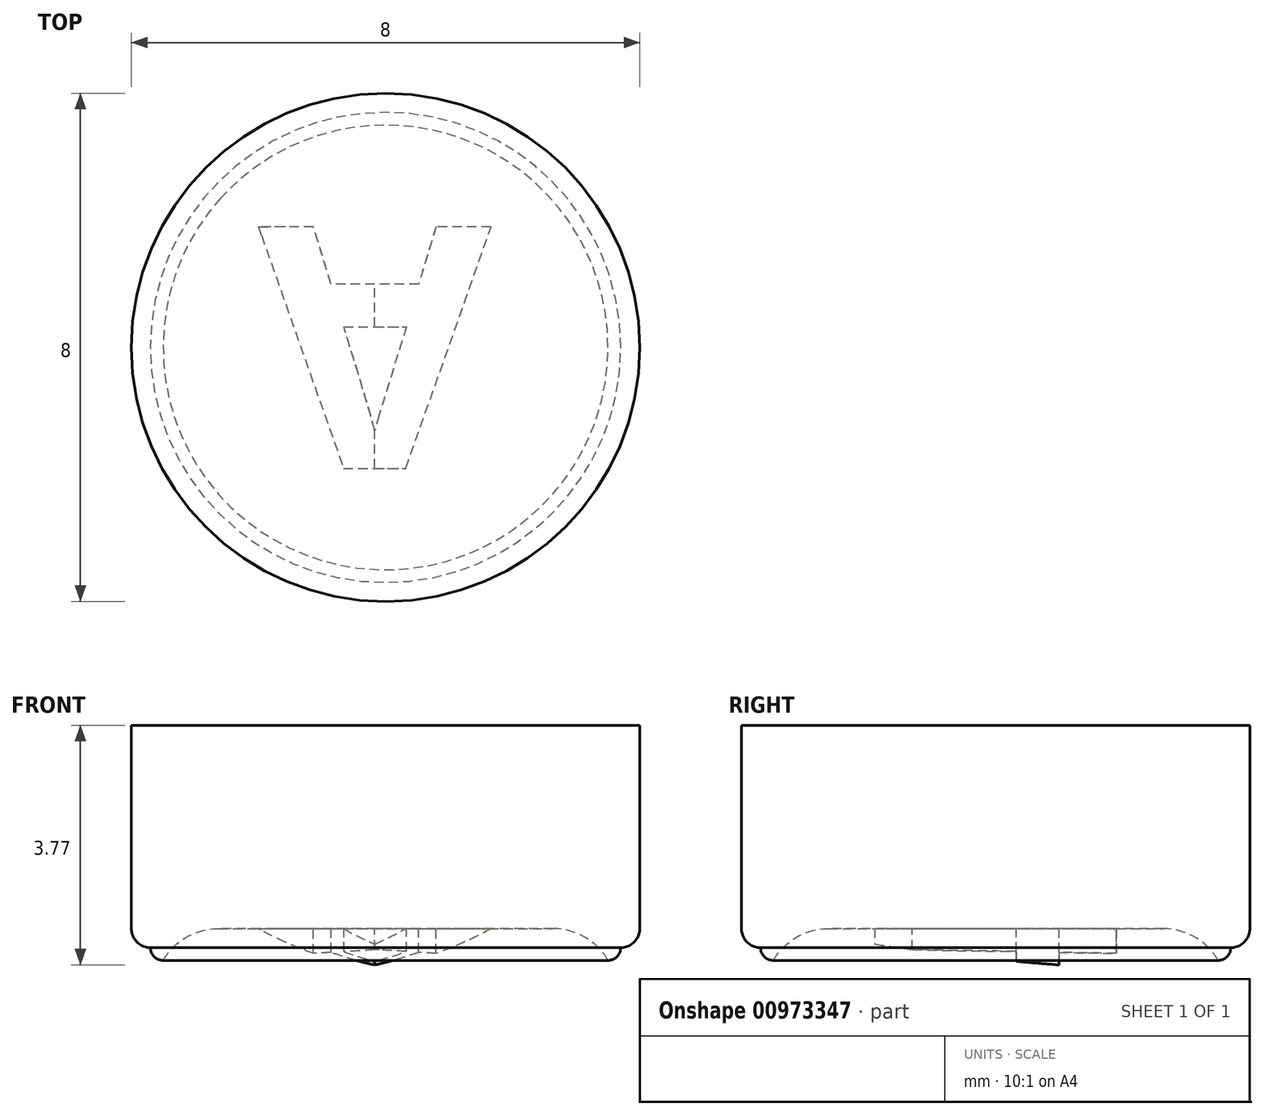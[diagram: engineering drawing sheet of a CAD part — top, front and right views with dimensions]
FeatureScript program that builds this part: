
annotation { "Feature Type Name" : "Feature", "Feature Type Description" : "" }
export const myFeature = defineFeature(function(context is Context, id is Id, definition is map)
    precondition{}
    {
        {
            var Q0;
            Q0=qCreatedBy(makeId("Top.planeOp"),FACE);
            var sketch = newSketch(context, id + "F0", { "sketchPlane" : qUnion([Q0])});
            skCircle(sketch, "E0", {"center": v(0, 0) * mm, "radius": 4 * mm});
            skSolve(sketch);
        }
        {
            var Q0;
            Q0=makeQuery(id+"F0.imprint","IMPRINT",FACE,{"disambiguationData":[TD([[makeQuery(id+"F0.imprint","IMPRINT",EDGE,{"derivedFrom":sQuery(id+"F0.wireOp",EDGE,"E0")}),1.0]])]});
            extrude(context, id + "F1", {"entities" : qUnion([Q0]), "depth" : 3.5 * mm, "offsetDistance" : 25 * mm});
        }
        {
            var Q0;
            Q0=makeQuery(id+"F1.opExtrude","CAP_EDGE",EDGE,{"disambiguationData":[OSD([sQuery(id+"F0.wireOp",EDGE,"E0")])],"isStart":false});
            fillet(context, id + "F2", {"entities" : qUnion([Q0]), "radius" : .3 * mm, "tangentPropagation" : true, "allowEdgeOverflow" : false});
        }
        {
            var Q0;
            Q0=makeQuery(id+"F1.opExtrude","CAP_FACE",FACE,{"disambiguationData":[OSD([sQuery(id+"F0.wireOp",EDGE,"E0")])],"isStart":false});
            extrude(context, id + "F3", {"entities" : qUnion([Q0]), "operationType" : NewBodyOperationType.ADD, "depth" : .2 * mm, "offsetDistance" : 25 * mm});
        }
        {
            var Q0;
            Q0=makeQuery(id+"F3.opExtrude","CAP_EDGE",EDGE,{"disambiguationData":[OSD([sQuery(id+"F0.wireOp",EDGE,"E0")])],"isStart":false});
            fillet(context, id + "F4", {"entities" : qUnion([Q0]), "radius" : .2 * mm, "tangentPropagation" : true, "allowEdgeOverflow" : false});
        }
        {
            var Q0;
            Q0=makeQuery(id+"F3.opExtrude","CAP_FACE",FACE,{"disambiguationData":[OSD([sQuery(id+"F0.wireOp",EDGE,"E0")])],"isStart":false});
            var sketch = newSketch(context, id + "F5", { "sketchPlane" : qUnion([Q0])});
            skText(sketch, "E1", { "text": "A", "fontName": "OpenSans-Bold.ttf"});
            const initialGuessF5  = {"E1": [-0.002, -0.0019, 1, 0, 0.00382]};
            skSetInitialGuess(sketch, initialGuessF5);
            skSolve(sketch);
        }
        {
            var Q0;
            Q0=makeQuery(id+"F5.imprint","IMPRINT",FACE,{"disambiguationData":[TD([[makeQuery(id+"F5.imprint","IMPRINT",EDGE,{"derivedFrom":sQuery(id+"F5.wireOp",EDGE,"E1.sketch_text.stroke-0")}),-1.0]])]});
            extrude(context, id + "F6", {"entities" : qUnion([Q0]), "operationType" : NewBodyOperationType.ADD, "depth" : 0.2 * mm, "offsetDistance" : 25 * mm});
        }
        {
            var Q0;
            Q0=makeQuery(id+"F6.boolean.opBoolean","SPLIT",FACE,{"disambiguationData":[TD([makeQuery(id+"F6.opExtrude","SWEPT_FACE",FACE,{"disambiguationData":[OSD([sQuery(id+"F5.wireOp",EDGE,"E1.sketch_text.stroke-8")])]})])],"derivedFrom":makeQuery(id+"F3.opExtrude","CAP_FACE",FACE,{"disambiguationData":[OSD([sQuery(id+"F0.wireOp",EDGE,"E0")])],"isStart":false})});
            extrude(context, id + "F7", {"entities" : qUnion([Q0]), "operationType" : NewBodyOperationType.REMOVE, "oppositeDirection" : true, "depth" : .5 * mm, "offsetDistance" : 25 * mm});
        }
        {
            var Q0;
            {var subQ0=sQuery(id+"F0.wireOp",EDGE,"E0");Q0=makeQuery(id+"F6.boolean.opBoolean","SPLIT",FACE,{"disambiguationData":[TD([makeQuery(id+"F4.opFillet","BLEND_FACE",FACE,{"disambiguationData":[OSD([subQ0])]})])],"derivedFrom":makeQuery(id+"F3.opExtrude","CAP_FACE",FACE,{"disambiguationData":[OSD([subQ0])],"isStart":false})});}
            extrude(context, id + "F8", {"entities" : qUnion([Q0]), "operationType" : NewBodyOperationType.REMOVE, "oppositeDirection" : true, "depth" : .5 * mm, "offsetDistance" : 25 * mm});
        }
        {
            var Q0;
            Q0=makeQuery(id+"F8.boolean.opBoolean","COPY",EDGE,{"derivedFrom":makeQuery(id+"F8.opExtrude","CAP_EDGE",EDGE,{"disambiguationData":[OSD([sQuery(id+"F0.wireOp",EDGE,"E0")])],"isStart":false})});
            fillet(context, id + "F9", {"entities" : qUnion([Q0]), "radius" : 1 * mm, "tangentPropagation" : true, "allowEdgeOverflow" : false});
        }
        {
            var Q0;
            Q0=makeQuery(id+"F6.opExtrude","CAP_EDGE",EDGE,{"disambiguationData":[OSD([sQuery(id+"F5.wireOp",EDGE,"E1.sketch_text.stroke-4")])],"isStart":false});
            var Q1;
            Q1=makeQuery(id+"F6.opExtrude","CAP_EDGE",EDGE,{"disambiguationData":[OSD([sQuery(id+"F5.wireOp",EDGE,"E1.sketch_text.stroke-6")])],"isStart":false});
            fillet(context, id + "F10", {"entities" : qUnion([Q0, Q1]), "radius" : 5 * mm, "tangentPropagation" : true, "allowEdgeOverflow" : false});
        }
        {
            var Q0;
            Q0=makeQuery(id+"F1.opExtrude","SWEPT_BODY",BODY,{"disambiguationData":[OSD([sQuery(id+"F0.wireOp",EDGE,"E0")])]});
            transform(context, id + "F11", {"entities" : qUnion([Q0]), "transformType" : TransformType.TRANSLATION_3D, "dx" : 0 * mm, "dy" : 0 * mm, "dz" : 30 * mm, "makeCopy" : false});
        }
        {
            var Q0;
            Q0=qCreatedBy(makeId("Top.planeOp"),FACE);
            var sketch = newSketch(context, id + "F12", { "sketchPlane" : qUnion([Q0])});
            skLineSegment(sketch, "E2.bottom", {"start": v(4.53, -4.2) * mm, "end": v(-4.53, -4.2) * mm});
            skLineSegment(sketch, "E2.top", {"start": v(4.53, 4.2) * mm, "end": v(-4.53, 4.2) * mm});
            skLineSegment(sketch, "E2.left", {"start": v(4.53, -4.2) * mm, "end": v(4.53, 4.2) * mm});
            skLineSegment(sketch, "E2.right", {"start": v(-4.53, -4.2) * mm, "end": v(-4.53, 4.2) * mm});
            skPoint(sketch, "E2.middle", {"position": v(0, 0) * mm});
            skSolve(sketch);
        }
        {
            var Q0;
            Q0=makeQuery(id+"F1.opExtrude","SWEPT_BODY",BODY,{"disambiguationData":[OSD([sQuery(id+"F0.wireOp",EDGE,"E0")])]});
            var Q1;
            Q1=sQuery(id+"F12.wireOp",EDGE,"E2.bottom");
            transform(context, id + "F13", {"entities" : qUnion([Q0]), "transformType" : TransformType.ROTATION, "transformAxis" : qUnion([Q1]), "angle" : 180 * degree, "makeCopy" : false});
        }
        {
            var Q0;
            Q0=makeQuery(id+"F1.opExtrude","SWEPT_BODY",BODY,{"disambiguationData":[OSD([sQuery(id+"F0.wireOp",EDGE,"E0")])]});
            transform(context, id + "F14", {"entities" : qUnion([Q0]), "transformType" : TransformType.TRANSLATION_3D, "dx" : 0 * mm, "dy" : 8 * mm, "dz" : 0 * mm, "makeCopy" : false});
        }
    });
